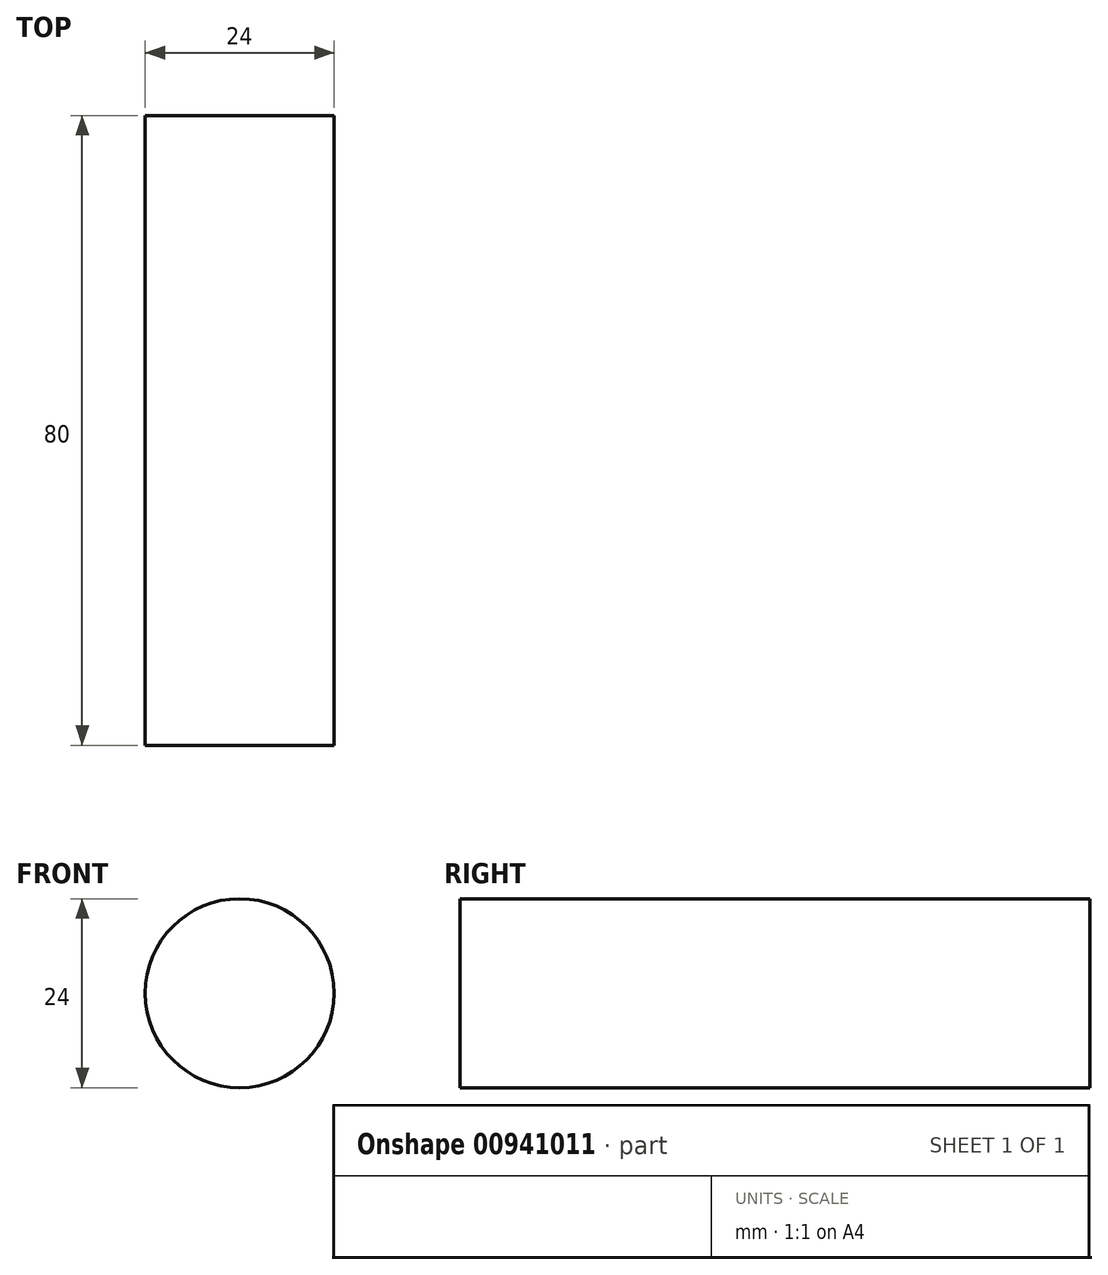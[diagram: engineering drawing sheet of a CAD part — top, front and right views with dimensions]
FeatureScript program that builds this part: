
annotation { "Feature Type Name" : "Feature", "Feature Type Description" : "" }
export const myFeature = defineFeature(function(context is Context, id is Id, definition is map)
    precondition{}
    {
        {
            var Q0;
            Q0=qCreatedBy(makeId("Front.planeOp"),FACE);
            var sketch = newSketch(context, id + "F0", { "sketchPlane" : qUnion([Q0])});
            skCircle(sketch, "E0", {"center": v(0.66, 0) * mm, "radius": 12 * mm});
            skSolve(sketch);
        }
        {
            var Q0;
            Q0 = qSketchRegion(id + "F0", true);
            extrude(context, id + "F1", {"entities" : qUnion([Q0]), "endBound" : BoundingType.SYMMETRIC, "depth" : 80 * mm, "offsetDistance" : 25 * mm});
        }
    });
